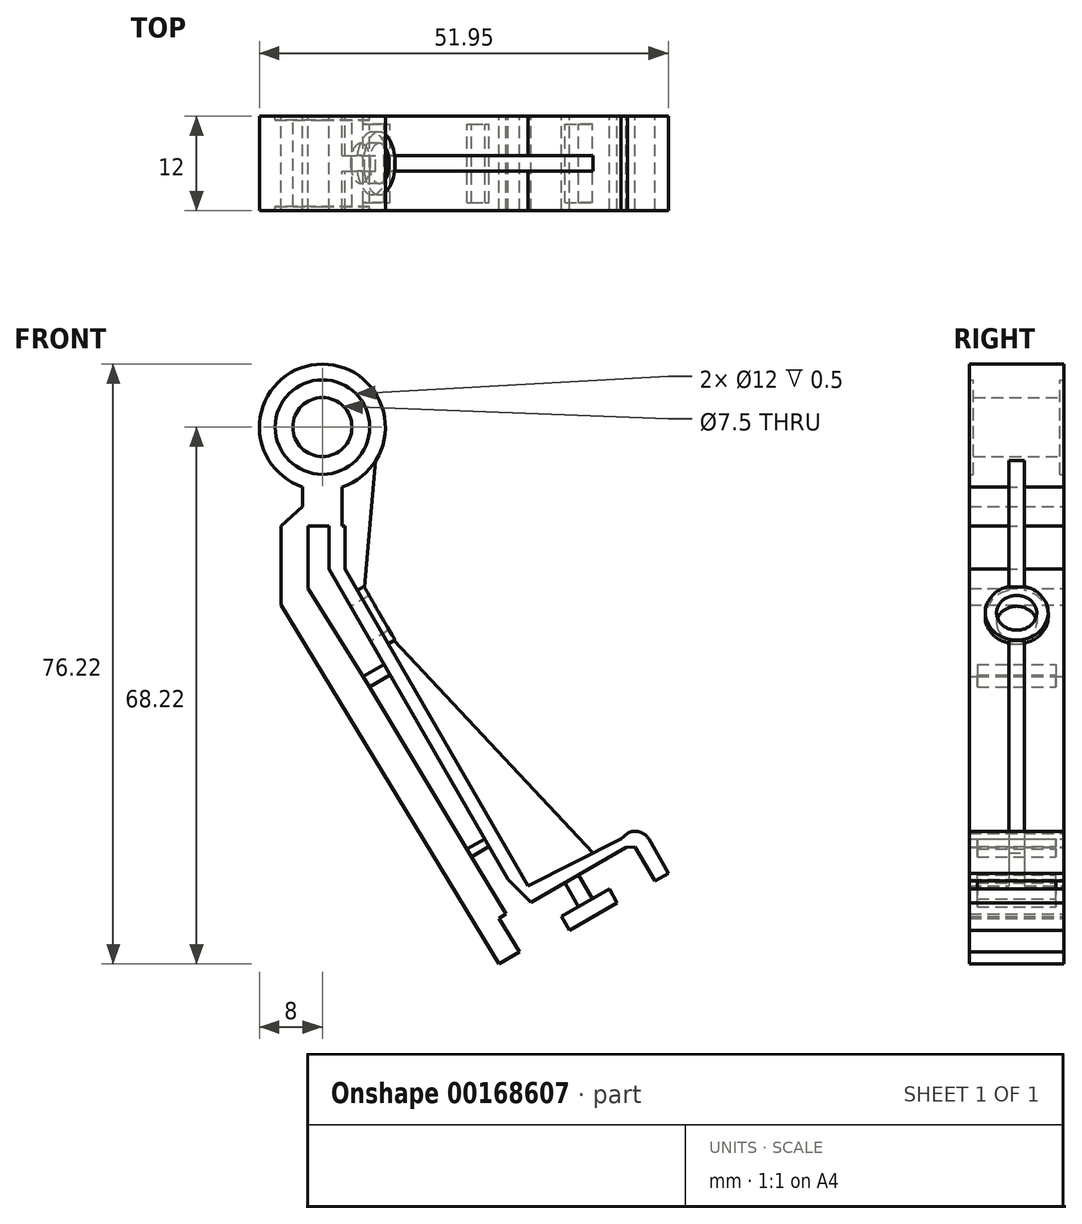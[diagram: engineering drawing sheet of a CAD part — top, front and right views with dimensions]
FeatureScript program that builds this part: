
annotation { "Feature Type Name" : "Feature", "Feature Type Description" : "" }
export const myFeature = defineFeature(function(context is Context, id is Id, definition is map)
    precondition{}
    {
        {
            var Q0;
            Q0=qCreatedBy(makeId("Front.planeOp"),FACE);
            var sketch = newSketch(context, id + "F0", { "sketchPlane" : qUnion([Q0])});
            skCircle(sketch, "E0", {"center": v(0, 0) * mm, "radius": 8 * mm});
            skCircle(sketch, "E1", {"center": v(0, 0) * mm, "radius": 6 * mm});
            skCircle(sketch, "E2", {"center": v(0, 0) * mm, "radius": 3.75 * mm});
            skLineSegment(sketch, "E3", {"start": v(-2.5, -7.6) * mm, "end": v(-2.5, -12.6) * mm});
            skLineSegment(sketch, "E4", {"start": v(-2.5, -12.6) * mm, "end": v(0, -12.6) * mm});
            skLineSegment(sketch, "E5", {"start": v(0, -12.6) * mm, "end": v(2.5, -12.6) * mm});
            skLineSegment(sketch, "E6", {"start": v(2.5, -12.6) * mm, "end": v(2.5, -7.6) * mm});
            skLineSegment(sketch, "E7.bottom", {"start": v(0, -12.6) * mm, "end": v(2.85, -12.6) * mm});
            skLineSegment(sketch, "E8", {"start": v(2.85, -18.04) * mm, "end": v(26.1, -58.3) * mm});
            skLineSegment(sketch, "E9.top", {"start": v(-5.25, -12.6) * mm, "end": v(-1.25, -12.6) * mm});
            skLineSegment(sketch, "E9.left", {"start": v(-5.25, -22.6) * mm, "end": v(-5.25, -12.6) * mm});
            skLineSegment(sketch, "E10.top", {"start": v(2.85, -12.6) * mm, "end": v(0, -12.6) * mm});
            skLineSegment(sketch, "E10.left", {"start": v(2.85, -18.04) * mm, "end": v(2.85, -12.6) * mm});
            skLineSegment(sketch, "E11.bottom", {"start": v(2.85, -12.6) * mm, "end": v(0.85, -12.6) * mm});
            skLineSegment(sketch, "E11.top", {"start": v(2.85, -18.04) * mm, "end": v(0.85, -18.04) * mm});
            skLineSegment(sketch, "E11.left", {"start": v(2.85, -12.6) * mm, "end": v(2.85, -18.04) * mm});
            skLineSegment(sketch, "E11.right", {"start": v(0.85, -12.6) * mm, "end": v(0.85, -18.04) * mm});
            skLineSegment(sketch, "E12", {"start": v(24.6, -59.17) * mm, "end": v(26.1, -58.3) * mm});
            skLineSegment(sketch, "E13", {"start": v(0.85, -18.04) * mm, "end": v(24.6, -59.17) * mm});
            skLineSegment(sketch, "E14", {"start": v(24.6, -59.17) * mm, "end": v(25.6, -60.9) * mm});
            skLineSegment(sketch, "E15", {"start": v(25.6, -60.9) * mm, "end": v(38.6, -53.4) * mm});
            skLineSegment(sketch, "E16", {"start": v(39.72, -53.35) * mm, "end": v(38.72, -51.62) * mm});
            skLineSegment(sketch, "E17", {"start": v(37.94, -52.3) * mm, "end": v(26.1, -58.3) * mm});
            skLineSegment(sketch, "E18", {"start": v(39.72, -53.35) * mm, "end": v(42.22, -57.68) * mm});
            skLineSegment(sketch, "E19", {"start": v(42.22, -57.68) * mm, "end": v(43.95, -56.68) * mm});
            skLineSegment(sketch, "E20", {"start": v(43.95, -56.68) * mm, "end": v(41.45, -52.35) * mm});
            skLineSegment(sketch, "E21", {"start": v(41.45, -52.35) * mm, "end": v(39.72, -53.35) * mm});
            skArc(sketch, "E22", {"start": v(41.45, -52.35) * mm, "mid": v(40.24, -51.42) * mm, "end": v(38.72, -51.62) * mm});
            skPoint(sketch, "E23", {"position": v(34.38, -54.1) * mm});
            skLineSegment(sketch, "E24", {"start": v(9.11, -27.14) * mm, "end": v(34.38, -54.1) * mm});
            skLineSegment(sketch, "E25", {"start": v(-5.25, -12.6) * mm, "end": v(-2.5, -10.1) * mm});
            skPoint(sketch, "E26", {"position": v(30.8, -57.9) * mm});
            skLineSegment(sketch, "E27", {"start": v(30.8, -57.9) * mm, "end": v(32.55, -60.94) * mm});
            skLineSegment(sketch, "E28", {"start": v(32.55, -60.94) * mm, "end": v(34.28, -59.94) * mm});
            skLineSegment(sketch, "E29", {"start": v(34.28, -59.94) * mm, "end": v(32.53, -56.9) * mm});
            skLineSegment(sketch, "E30", {"start": v(32.55, -60.94) * mm, "end": v(30.38, -62.19) * mm});
            skLineSegment(sketch, "E31", {"start": v(30.38, -62.19) * mm, "end": v(31.38, -63.92) * mm});
            skLineSegment(sketch, "E32", {"start": v(31.38, -63.92) * mm, "end": v(37.44, -60.42) * mm});
            skLineSegment(sketch, "E33", {"start": v(37.44, -60.42) * mm, "end": v(36.44, -58.69) * mm});
            skLineSegment(sketch, "E34", {"start": v(36.44, -58.69) * mm, "end": v(34.28, -59.94) * mm});
            skPoint(sketch, "E35", {"position": v(7.85, -30.16) * mm});
            skLineSegment(sketch, "E36", {"start": v(7.85, -30.16) * mm, "end": v(5.19, -31.7) * mm});
            skLineSegment(sketch, "E37", {"start": v(5.19, -31.7) * mm, "end": v(5.95, -32.99) * mm});
            skLineSegment(sketch, "E38", {"start": v(5.95, -32.99) * mm, "end": v(8.6, -31.46) * mm});
            skLineSegment(sketch, "E39", {"start": v(19.7, -55.87) * mm, "end": v(18.93, -54.58) * mm});
            skLineSegment(sketch, "E40", {"start": v(18.93, -54.58) * mm, "end": v(21.2, -53.27) * mm});
            skLineSegment(sketch, "E41", {"start": v(21.2, -53.27) * mm, "end": v(21.85, -54.41) * mm});
            skPoint(sketch, "E42", {"position": v(8.35, -27.56) * mm});
            skLineSegment(sketch, "E43", {"start": v(9.11, -27.14) * mm, "end": v(8.35, -27.56) * mm});
            skLineSegment(sketch, "E44", {"start": v(22.43, -68.22) * mm, "end": v(25.86, -66.16) * mm});
            skLineSegment(sketch, "E45", {"start": v(-5.25, -22.6) * mm, "end": v(22.43, -68.22) * mm});
            skLineSegment(sketch, "E46", {"start": v(-5.25, -22.6) * mm, "end": v(-1.83, -20.52) * mm});
            skLineSegment(sketch, "E47", {"start": v(-1.83, -20.52) * mm, "end": v(5.19, -31.7) * mm});
            skLineSegment(sketch, "E48", {"start": v(5.95, -32.99) * mm, "end": v(18.93, -54.58) * mm});
            skLineSegment(sketch, "E49", {"start": v(19.7, -55.87) * mm, "end": v(25.86, -66.16) * mm});
            skLineSegment(sketch, "E50", {"start": v(-1.83, -20.52) * mm, "end": v(-1.83, -12.6) * mm});
            skLineSegment(sketch, "E51", {"start": v(25, -66.68) * mm, "end": v(22.44, -62.39) * mm});
            skLineSegment(sketch, "E52", {"start": v(22.44, -62.39) * mm, "end": v(23.3, -61.87) * mm});
            skLineSegment(sketch, "E53", {"start": v(23.6, -57.44) * mm, "end": v(26.47, -60.4) * mm});
            skLineSegment(sketch, "E54", {"start": v(4.47, -20.84) * mm, "end": v(5.33, -20.34) * mm});
            skLineSegment(sketch, "E55", {"start": v(5.33, -20.34) * mm, "end": v(6.76, -4.28) * mm});
            skLineSegment(sketch, "E56", {"start": v(18.35, -53.62) * mm, "end": v(20.63, -52.3) * mm});
            skPoint(sketch, "E57", {"position": v(39.7, -53.34) * mm});
            skLineSegment(sketch, "E58", {"start": v(37.94, -52.3) * mm, "end": v(38.72, -51.62) * mm});
            skLineSegment(sketch, "E59", {"start": v(38.6, -53.4) * mm, "end": v(39.72, -53.35) * mm});
            skSolve(sketch);
        }
        {
            var Q0;
            Q0=makeQuery(id+"F0.imprint","IMPRINT",FACE,{"disambiguationData":[TD([[makeQuery(id+"F0.imprint","IMPRINT",EDGE,{"derivedFrom":sQuery(id+"F0.wireOp",EDGE,"E1")}),-1.0]])]});
            var Q1;
            {var subQ0=sQuery(id+"F0.wireOp",EDGE,"E4");Q1=makeQuery(id+"F0.imprint","IMPRINT",FACE,{"disambiguationData":[TD([[makeQuery(id+"F0.imprint","IMPRINT",EDGE,{"derivedFrom":subQ0}),1.0]])]});}
            var Q2;
            {var subQ3=sQuery(id+"F0.wireOp",EDGE,"E25");Q2=makeQuery(id+"F0.imprint","IMPRINT",FACE,{"disambiguationData":[TD([[makeQuery(id+"F0.imprint","IMPRINT",EDGE,{"derivedFrom":subQ3}),-1.0]])]});}
            var Q3;
            Q3=makeQuery(id+"F0.imprint","IMPRINT",FACE,{"disambiguationData":[TD([[makeQuery(id+"F0.imprint","IMPRINT",EDGE,{"derivedFrom":sQuery(id+"F0.wireOp",EDGE,"E9.bottom")}),1.0]])]});
            var Q4;
            Q4=makeQuery(id+"F0.imprint","IMPRINT",FACE,{"disambiguationData":[TD([[makeQuery(id+"F0.imprint","IMPRINT",EDGE,{"derivedFrom":sQuery(id+"F0.wireOp",EDGE,"E11.top")}),-1.0]])]});
            var Q5;
            Q5=makeQuery(id+"F0.imprint","IMPRINT",FACE,{"disambiguationData":[TD([[makeQuery(id+"F0.imprint","IMPRINT",EDGE,{"derivedFrom":sQuery(id+"F0.wireOp",EDGE,"J5m7dxuD-NJp7-o8Hf-iOgj-6lMcWnvu8OeF")}),1.0]])]});
            var Q6;
            {var subQ0=sQuery(id+"F0.wireOp",EDGE,"E11.top");Q6=makeQuery(id+"F0.imprint","IMPRINT",FACE,{"disambiguationData":[TD([[makeQuery(id+"F0.imprint","IMPRINT",EDGE,{"derivedFrom":subQ0}),1.0]])]});}
            var Q7;
            Q7=makeQuery(id+"F0.imprint","IMPRINT",FACE,{"disambiguationData":[TD([[makeQuery(id+"F0.imprint","IMPRINT",EDGE,{"derivedFrom":sQuery(id+"F0.wireOp",EDGE,"E16")}),-1.0]])]});
            var Q8;
            Q8=makeQuery(id+"F0.imprint","IMPRINT",FACE,{"disambiguationData":[TD([[makeQuery(id+"F0.imprint","IMPRINT",EDGE,{"derivedFrom":sQuery(id+"F0.wireOp",EDGE,"E18")}),1.0]])]});
            var Q9;
            Q9=makeQuery(id+"F0.imprint","IMPRINT",FACE,{"disambiguationData":[TD([[makeQuery(id+"F0.imprint","IMPRINT",EDGE,{"derivedFrom":sQuery(id+"F0.wireOp",EDGE,"E28")}),-1.0]])]});
            var Q10;
            {var subQ1=sQuery(id+"F0.wireOp",EDGE,"E9.left");Q10=makeQuery(id+"F0.imprint","IMPRINT",FACE,{"disambiguationData":[TD([[makeQuery(id+"F0.imprint","IMPRINT",EDGE,{"derivedFrom":subQ1}),-1.0]])]});}
            var Q11;
            {var subQ0=sQuery(id+"F0.wireOp",EDGE,"E37");Q11=makeQuery(id+"F0.imprint","IMPRINT",FACE,{"disambiguationData":[TD([[makeQuery(id+"F0.imprint","IMPRINT",EDGE,{"derivedFrom":subQ0}),-1.0]])]});}
            var Q12;
            {var subQ0=sQuery(id+"F0.wireOp",EDGE,"E16");Q12=makeQuery(id+"F0.imprint","IMPRINT",FACE,{"disambiguationData":[TD([[makeQuery(id+"F0.imprint","IMPRINT",EDGE,{"derivedFrom":subQ0}),1.0]])]});}
            extrude(context, id + "F1", {"entities" : qUnion([Q0, Q1, Q2, Q3, Q4, Q5, Q6, Q7, Q8, Q9, Q10, Q11, Q12]), "endBound" : BoundingType.SYMMETRIC, "depth" : 12 * mm});
        }
        {
            var Q0;
            {var subQ0=sQuery(id+"F0.wireOp",EDGE,"E27");Q0=makeQuery(id+"F0.imprint","IMPRINT",FACE,{"disambiguationData":[TD([[makeQuery(id+"F0.imprint","IMPRINT",EDGE,{"derivedFrom":subQ0}),1.0]])]});}
            var Q1;
            Q1=makeQuery(id+"F0.imprint","IMPRINT",FACE,{"disambiguationData":[TD([[makeQuery(id+"F0.imprint","IMPRINT",EDGE,{"derivedFrom":sQuery(id+"F0.wireOp",EDGE,"oUjv94iJ-bGj4-jKm2-UY1X-5GEbn7oFcZo6")}),-1.0]])]});
            var Q2;
            {var subQ0=sQuery(id+"F0.wireOp",EDGE,"E36");Q2=makeQuery(id+"F0.imprint","IMPRINT",FACE,{"disambiguationData":[TD([[makeQuery(id+"F0.imprint","IMPRINT",EDGE,{"derivedFrom":subQ0}),1.0]])]});}
            var Q3;
            {var subQ0=sQuery(id+"F0.wireOp",EDGE,"E40");Q3=makeQuery(id+"F0.imprint","IMPRINT",FACE,{"disambiguationData":[TD([[makeQuery(id+"F0.imprint","IMPRINT",EDGE,{"derivedFrom":subQ0}),1.0]])]});}
            extrude(context, id + "F2", {"entities" : qUnion([Q0, Q1, Q2, Q3]), "operationType" : NewBodyOperationType.ADD, "endBound" : BoundingType.SYMMETRIC, "depth" : 10 * mm});
        }
        {
            var Q0;
            Q0=makeQuery(id+"F0.imprint","IMPRINT",FACE,{"disambiguationData":[TD([[makeQuery(id+"F0.imprint","IMPRINT",EDGE,{"derivedFrom":sQuery(id+"F0.wireOp",EDGE,"E1")}),1.0]])]});
            extrude(context, id + "F3", {"entities" : qUnion([Q0]), "operationType" : NewBodyOperationType.ADD, "endBound" : BoundingType.SYMMETRIC, "depth" : 11 * mm});
        }
        {
            var Q0;
            {var subQ1=sQuery(id+"F0.wireOp",EDGE,"E6");Q0=makeQuery(id+"F0.imprint","IMPRINT",FACE,{"disambiguationData":[TD([[makeQuery(id+"F0.imprint","IMPRINT",EDGE,{"derivedFrom":subQ1}),-1.0]])]});}
            var Q1;
            {var subQ3=sQuery(id+"F0.wireOp",EDGE,"aCOTb3oc-ZVIg-T0J8-2oBW-VlTkToRy8gR5");Q1=makeQuery(id+"F0.imprint","IMPRINT",FACE,{"disambiguationData":[TD([[makeQuery(id+"F0.imprint","IMPRINT",EDGE,{"derivedFrom":subQ3}),1.0]])]});}
            var Q2;
            {var subQ4=sQuery(id+"F0.wireOp",EDGE,"E24");Q2=makeQuery(id+"F0.imprint","IMPRINT",FACE,{"disambiguationData":[TD([[makeQuery(id+"F0.imprint","IMPRINT",EDGE,{"derivedFrom":subQ4}),-1.0]])]});}
            extrude(context, id + "F4", {"entities" : qUnion([Q0, Q1, Q2]), "operationType" : NewBodyOperationType.ADD, "endBound" : BoundingType.SYMMETRIC, "depth" : 2 * mm});
        }
        {
            var Q0;
            Q0=makeQuery(id+"F1.opExtrude","SWEPT_FACE",FACE,{"disambiguationData":[OSD([sQuery(id+"F0.wireOp",EDGE,"E8")])]});
            var sketch = newSketch(context, id + "F5", { "sketchPlane" : qUnion([Q0])});
            skCircle(sketch, "E60", {"center": v(0, -24.05) * mm, "radius": 4 * mm});
            skPoint(sketch, "E60.first.point", {"position": v(0, -28.05) * mm});
            skPoint(sketch, "E60.second.point", {"position": v(0, -28.05) * mm});
            skPoint(sketch, "E60.third.point", {"position": v(1.79, -27.63) * mm});
            skCircle(sketch, "E61", {"center": v(0, -24.05) * mm, "radius": 2.55 * mm});
            skSolve(sketch);
        }
        {
            var Q0;
            Q0=makeQuery(id+"F5.imprint","IMPRINT",FACE,{"disambiguationData":[TD([[makeQuery(id+"F5.imprint","IMPRINT",EDGE,{"derivedFrom":sQuery(id+"F5.wireOp",EDGE,"E61")}),-1.0]])]});
            extrude(context, id + "F6", {"entities" : qUnion([Q0]), "operationType" : NewBodyOperationType.ADD, "depth" : 1 * mm});
        }
        {
            var Q0;
            Q0=makeQuery(id+"F5.imprint","IMPRINT",FACE,{"disambiguationData":[TD([[makeQuery(id+"F5.imprint","IMPRINT",EDGE,{"derivedFrom":sQuery(id+"F5.wireOp",EDGE,"E61")}),1.0]])]});
            extrude(context, id + "F7", {"entities" : qUnion([Q0]), "operationType" : NewBodyOperationType.REMOVE, "oppositeDirection" : true, "depth" : 3 * mm});
        }
    });
